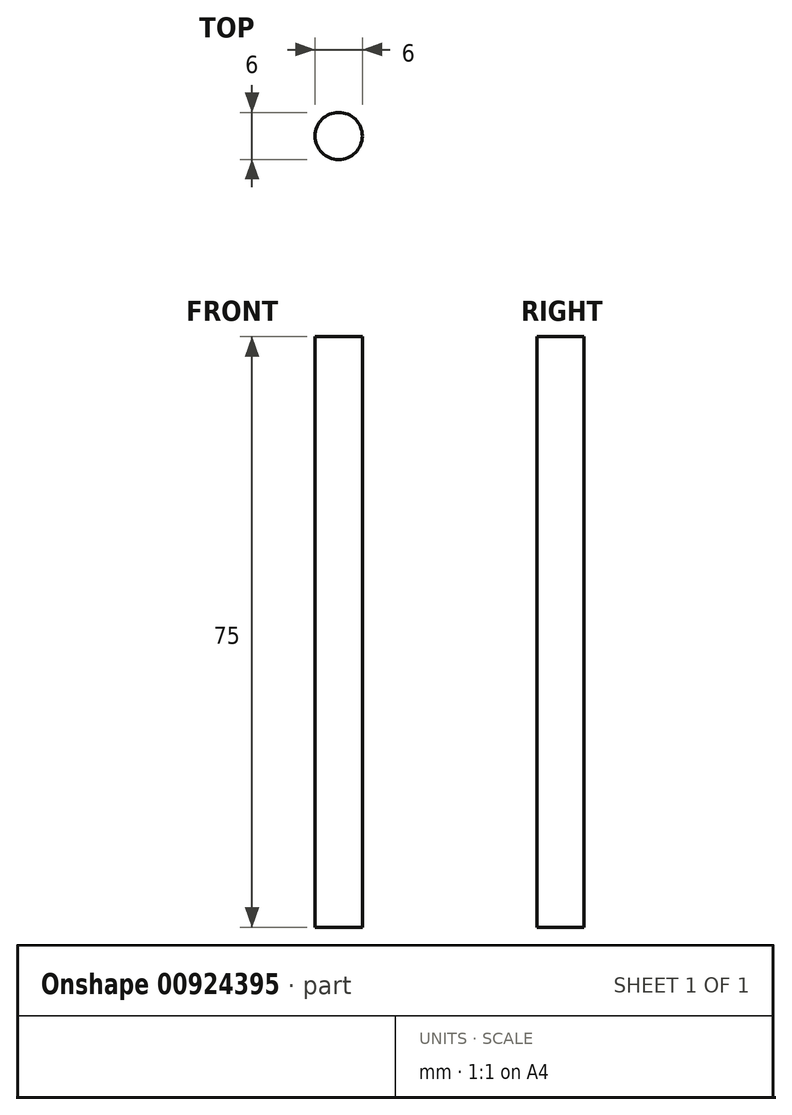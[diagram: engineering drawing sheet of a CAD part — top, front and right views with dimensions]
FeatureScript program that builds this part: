
annotation { "Feature Type Name" : "Feature", "Feature Type Description" : "" }
export const myFeature = defineFeature(function(context is Context, id is Id, definition is map)
    precondition{}
    {
        {
            var Q0;
            Q0=qCreatedBy(makeId("Top.planeOp"),FACE);
            var sketch = newSketch(context, id + "F0", { "sketchPlane" : qUnion([Q0])});
            skCircle(sketch, "E0", {"center": v(-28.76, 28.58) * mm, "radius": 3 * mm});
            skSolve(sketch);
        }
        {
            var Q0;
            Q0 = qSketchRegion(id + "F0", true);
            extrude(context, id + "F1", {"entities" : qUnion([Q0]), "depth" : 75 * mm, "offsetDistance" : 25 * mm});
        }
    });
